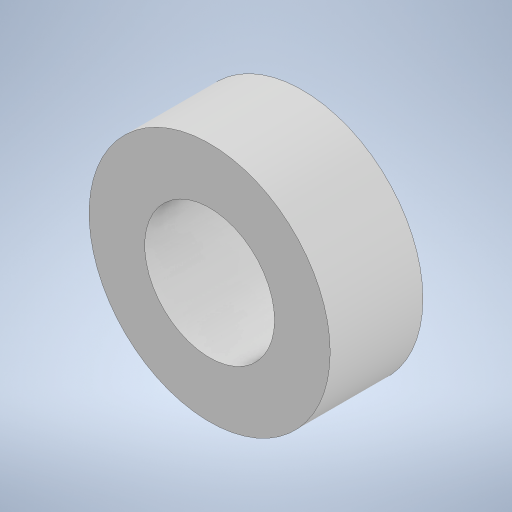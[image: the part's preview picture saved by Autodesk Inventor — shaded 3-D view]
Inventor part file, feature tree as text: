
AUTODESK INVENTOR PART (.ipt)
format: ipt  version: 2024 (Build 280153000, 153)  size: 212,480 bytes
history: native  units: mm
features: extrude x1, sketch x1
ambient origin geometry x8: Origin, YZ Plane, XZ Plane, XY Plane, X Axis, Y Axis, Z Axis, Center Point
bodies: Solid1 (feature_tree)
feature tree (2):
  extrude  "Extrusion1"  Depth=5.0mm
  sketch  "Sketch1"  dims[d0=7.0mm d1=13.0mm d2=5.0mm d3=0.0mm]
